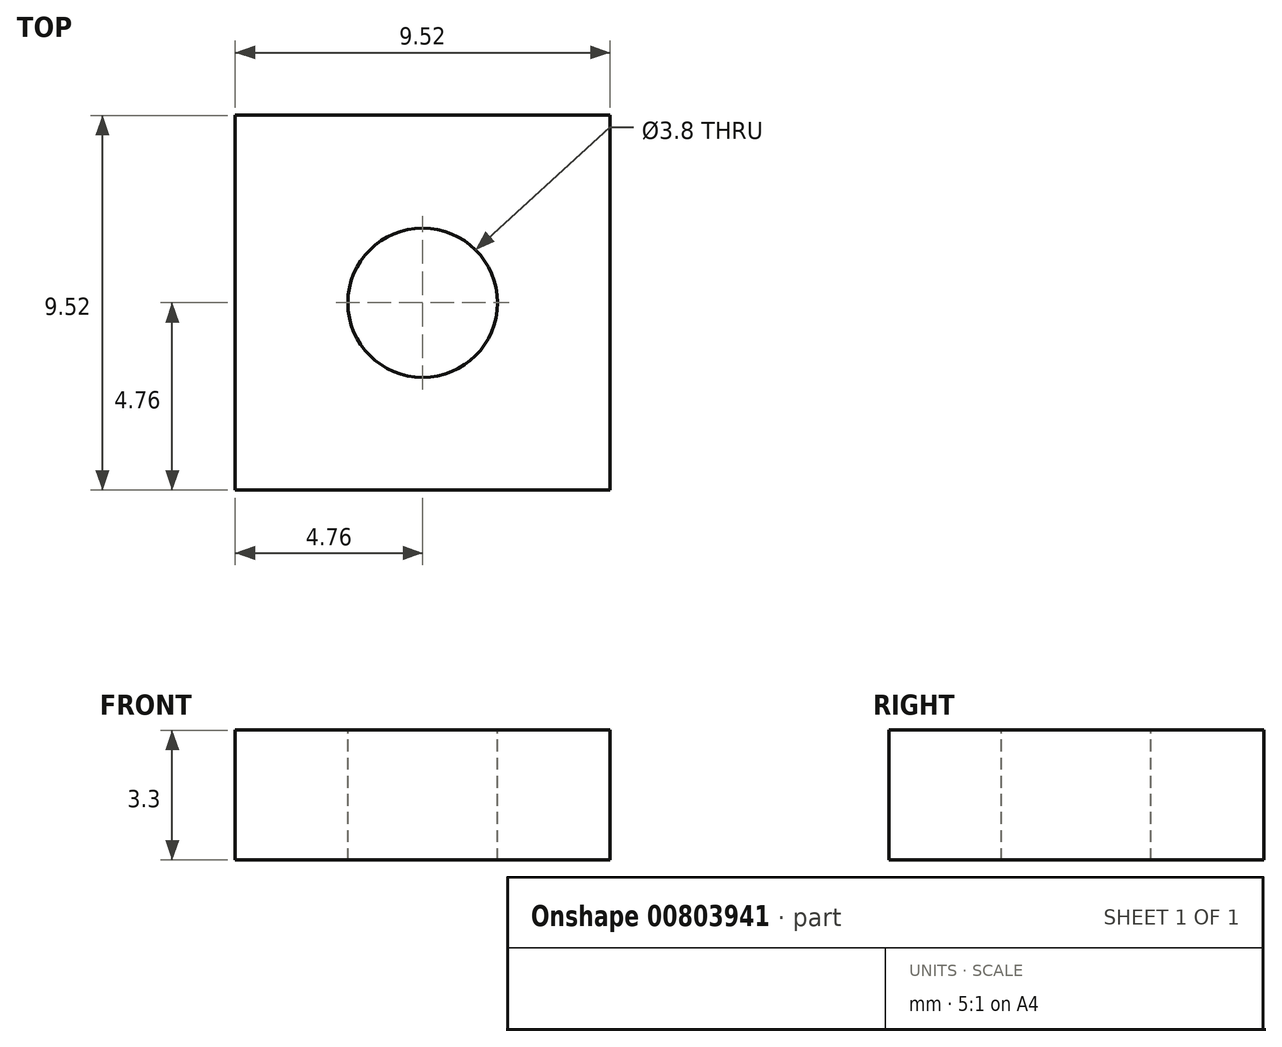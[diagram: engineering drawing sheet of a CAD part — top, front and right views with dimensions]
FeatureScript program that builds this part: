
annotation { "Feature Type Name" : "Feature", "Feature Type Description" : "" }
export const myFeature = defineFeature(function(context is Context, id is Id, definition is map)
    precondition{}
    {
        {
            var Q0;
            Q0=qCreatedBy(makeId("Top.planeOp"),FACE);
            var sketch = newSketch(context, id + "F0", { "sketchPlane" : qUnion([Q0])});
            skLineSegment(sketch, "E0", {"start": v(0, 4.76) * mm, "end": v(0, -4.76) * mm, "construction": true});
            skLineSegment(sketch, "E1", {"start": v(-4.76, 0) * mm, "end": v(4.76, 0) * mm, "construction": true});
            skLineSegment(sketch, "E2.bottom", {"start": v(-4.76, 4.76) * mm, "end": v(4.76, 4.76) * mm});
            skLineSegment(sketch, "E2.top", {"start": v(-4.76, -4.76) * mm, "end": v(4.76, -4.76) * mm});
            skLineSegment(sketch, "E2.left", {"start": v(-4.76, 4.76) * mm, "end": v(-4.76, -4.76) * mm});
            skLineSegment(sketch, "E2.right", {"start": v(4.76, 4.76) * mm, "end": v(4.76, -4.76) * mm});
            skSolve(sketch);
        }
        {
            var Q0;
            Q0 = qSketchRegion(id + "F0", true);
            extrude(context, id + "F1", {"entities" : qUnion([Q0]), "depth" : 3.3 * mm, "offsetDistance" : 25.4 * mm});
        }
        {
            var Q0;
            Q0=makeQuery(id+"F1.opExtrude","CAP_FACE",FACE,{"disambiguationData":[OSD([sQuery(id+"F0.wireOp",EDGE,"E2.bottom"),sQuery(id+"F0.wireOp",EDGE,"E2.top"),sQuery(id+"F0.wireOp",EDGE,"E2.left"),sQuery(id+"F0.wireOp",EDGE,"E2.right")])],"isStart":false});
            var sketch = newSketch(context, id + "F2", { "sketchPlane" : qUnion([Q0])});
            skPoint(sketch, "E3", {"position": v(0, 0) * mm});
            skSolve(sketch);
        }
        {
            var Q0;
            Q0=sQuery(id+"F2.wireOp",VERTEX,"E3");
            var Q1;
            Q1=makeQuery(id+"F1.opExtrude","SWEPT_BODY",BODY,{"disambiguationData":[OSD([sQuery(id+"F0.wireOp",EDGE,"E2.bottom"),sQuery(id+"F0.wireOp",EDGE,"E2.top"),sQuery(id+"F0.wireOp",EDGE,"E2.left"),sQuery(id+"F0.wireOp",EDGE,"E2.right")])]});
            hole(context, id + "F3", {"style" : HoleStyle.SIMPLE, "endStyle" : HoleEndStyle.THROUGH, "standardTappedOrClearance" : lookupTablePath({ "standard" : "ANSI", "engagement" : "75%", "pitch" : "24 tpi", "size" : "#10", "type" : "Tapped" }), "standardBlindInLast" : lookupTablePath({ "standard" : "ANSI", "engagement" : "75%", "pitch" : "24 tpi", "size" : "#10", "type" : "Tapped" }), "holeDiameter" : 3.8 * mm, "majorDiameter" : 4.83 * mm, "showTappedDepth" : true, "isTappedThrough" : true, "tappedDepth" : 12.7 * mm, "tapClearance" : 3, "startFromSketch" : true, "locations" : qUnion([Q0]), "scope" : qUnion([Q1])});
        }
    });
